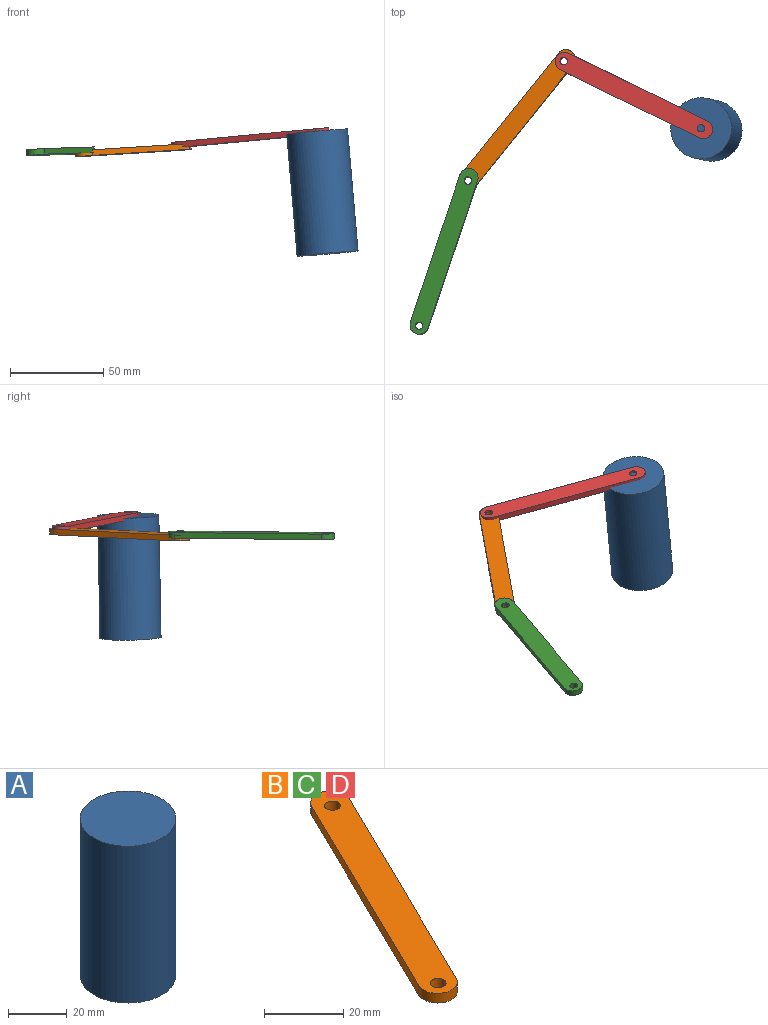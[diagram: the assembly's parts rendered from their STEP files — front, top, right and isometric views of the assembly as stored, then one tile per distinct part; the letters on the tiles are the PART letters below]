
ASSEMBLY  parts=4 mates=3
PART A: 3 faces, bbox 32.7x32.7x65.5 mm
  f0: cylinder r=16.36mm len=65.53mm, axis (0,0,-1), area 6734.8mm2, adj f1,f2
  f1: plane 32.71x32.71mm, normal (0,0,1), area 840.5mm2, adj f0
  f2: plane 32.71x32.71mm, normal (0,0,-1), area 840.5mm2, adj f0
PART B: 8 faces, bbox 46.6x84.8x3 mm
  f0: cylinder r=2mm len=4mm, axis (0,0,-1), area 37.7mm2, adj f5,f6
  f1: plane 74.6x36.39mm, normal (0.9,-0.44,0), area 249mm2, adj f2,f4,f5,f6
  f2: cylinder r=5mm len=9.49mm, axis (0,0,-1), area 47.1mm2, adj f1,f3,f5,f6
  f3: plane 74.6x36.39mm, normal (-0.9,0.44,0), area 249mm2, adj f2,f4,f5,f6
  f4: cylinder r=5mm len=9.49mm, axis (0,0,-1), area 47.1mm2, adj f1,f3,f5,f6
  f5: plane 84.78x46.57mm, normal (0,0,1), area 883.4mm2, adj f0,f1,f2,f3,f4,f7
  f6: plane 84.78x46.57mm, normal (0,0,-1), area 883.4mm2, adj f0,f1,f2,f3,f4,f7
  f7: cylinder r=2mm len=4mm, axis (0,0,-1), area 37.7mm2, adj f5,f6
PART C: same geometry as B
PART D: same geometry as B
PLACE A rot(axis=(-0.21,-0.98,0),5deg) t=(-113.34,-32.3,27.88)mm
PLACE B rot(axis=(-0.04,-0.36,-0.93),13.8deg) t=(-6.75,-144.05,101.81)mm
PLACE C rot(axis=(-0.15,-0.54,0.83),8.9deg) t=(-7.98,-118,102.73)mm
PLACE D rot(axis=(0.03,-0.05,-1),90.1deg) t=(-289.98,-256.68,81.12)mm
MATE revolute D.f7 <-> B.f0  axis (0.09,-0.02,-1) through (-232.73,41.75,80.6)mm
MATE revolute C.f0 <-> B.f7  axis (0.09,-0.02,-1) through (-284.16,-22.11,78.86)mm
MATE fastened D.f0 <-> A.f0  axis (0.09,-0.02,-1) through (-159.45,5.88,89.03)mm
